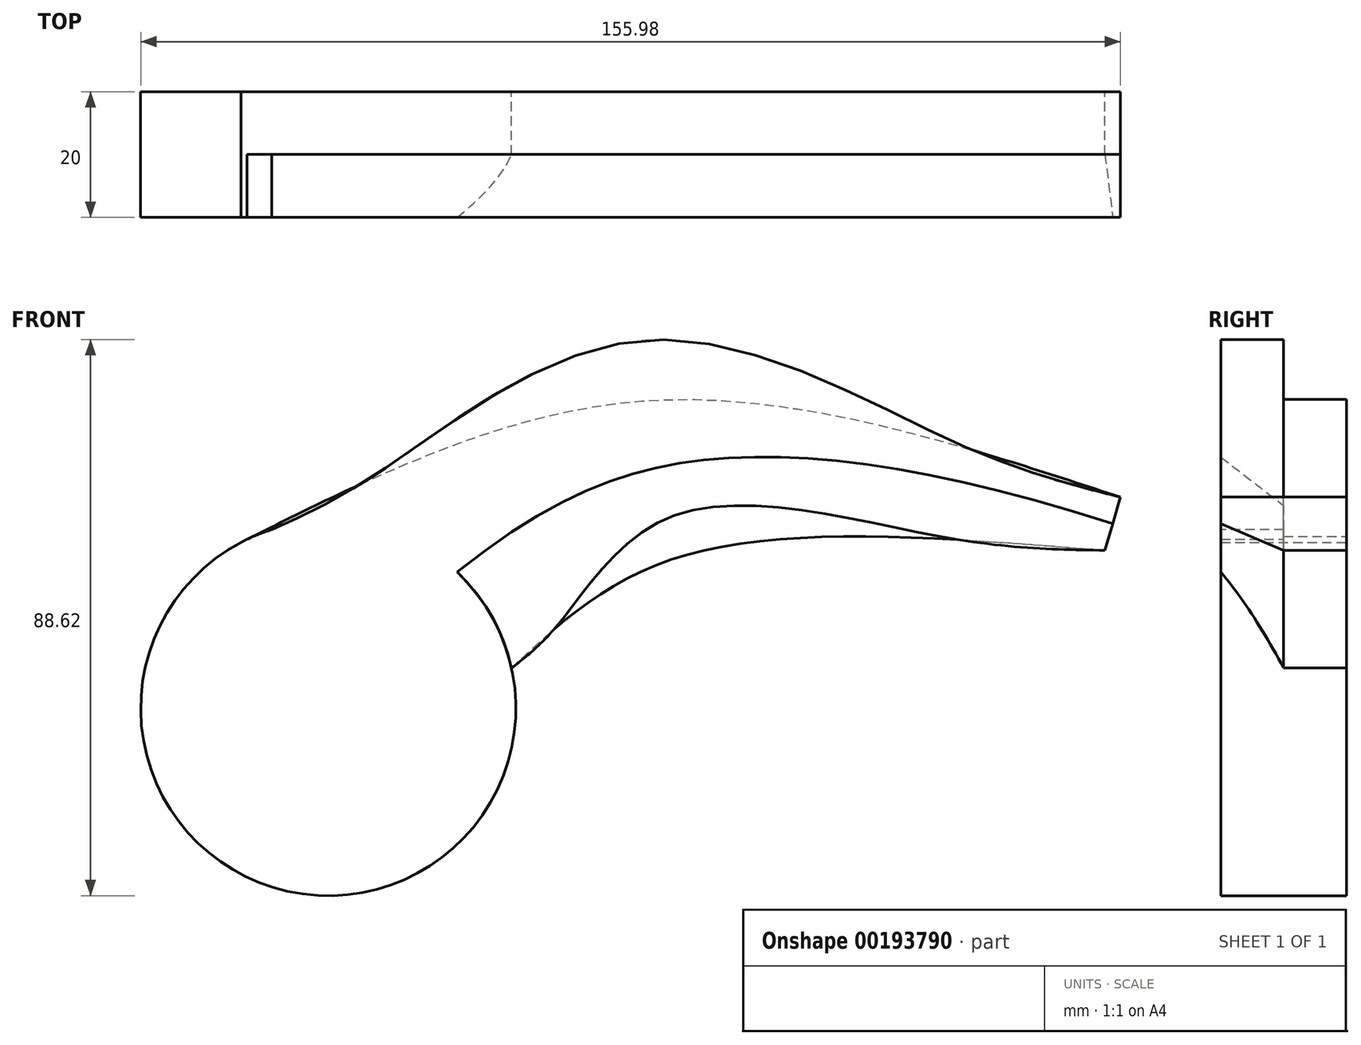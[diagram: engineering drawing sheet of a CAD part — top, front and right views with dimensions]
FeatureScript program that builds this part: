
annotation { "Feature Type Name" : "Feature", "Feature Type Description" : "" }
export const myFeature = defineFeature(function(context is Context, id is Id, definition is map)
    precondition{}
    {
        {
            var Q0;
            Q0=qCreatedBy(makeId("Front.planeOp"),FACE);
            var sketch = newSketch(context, id + "F0", { "sketchPlane" : qUnion([Q0])});
            skCircle(sketch, "E0", {"center": v(-61.69, -9.69) * mm, "radius": 29.87 * mm});
            skFitSpline(sketch, "E1", {"points": [v(-75.58, 16.75) * mm, v(-11.1, 39.34) * mm, v(64.43, 23.96) * mm], "startDerivative": vector(129.61, 65.17) * mm, "endDerivative": vector(150.18, -49.54) * mm});
            skFitSpline(sketch, "E2", {"points": [v(-32.52, -3.28) * mm, v(-5.98, 14.38) * mm, v(61.98, 15.5) * mm], "startDerivative": vector(55.34, 51.9) * mm, "endDerivative": vector(129.12, -10.46) * mm});
            skLineSegment(sketch, "E3", {"start": v(61.98, 15.5) * mm, "end": v(64.43, 23.96) * mm});
            skSolve(sketch);
        }
        {
            var Q0;
            {var subQ0=sQuery(id+"F0.wireOp",EDGE,"E0");var subQ1=makeQuery(id+"F0.imprint","INTERSECT",VERTEX,{"derivedFrom":[subQ0,sQuery(id+"F0.wireOp",EDGE,"E2")]});Q0=makeQuery(id+"F0.imprint","IMPRINT",FACE,{"disambiguationData":[TD([[makeQuery(id+"F0.imprint","IMPRINT",EDGE,{"disambiguationData":[TD([[subQ1,-1.0]])],"derivedFrom":subQ0}),1.0]])]});}
            cPlane(context, id + "F1", {"entities" : qUnion([Q0]), "cplaneType" : CPlaneType.OFFSET, "offset" : 10 * mm, "width" : 150 * mm, "height" : 150 * mm});
        }
        {
            var Q0;
            Q0=qCreatedBy(id+"F1.planeOp",FACE);
            cPlane(context, id + "F2", {"entities" : qUnion([Q0]), "cplaneType" : CPlaneType.OFFSET, "offset" : 10 * mm, "width" : 150 * mm, "height" : 150 * mm});
        }
        {
            var Q0;
            Q0=qCreatedBy(id+"F1.planeOp",FACE);
            var sketch = newSketch(context, id + "F3", { "sketchPlane" : qUnion([Q0])});
            skFitSpline(sketch, "E4.0", {"points": [v(-32.52, -3.28) * mm, v(-25.02, 3.75) * mm, v(-6.6, 21.05) * mm, v(36.44, 17.56) * mm, v(61.98, 15.5) * mm]});
            skFitSpline(sketch, "E4.2", {"points": [v(-75.58, 16.75) * mm, v(-54.63, 27.29) * mm, v(-11.4, 48.97) * mm, v(38.65, 32.47) * mm, v(64.43, 23.96) * mm]});
            skLineSegment(sketch, "E4.3", {"start": v(61.98, 15.5) * mm, "end": v(64.43, 23.96) * mm});
            skArc(sketch, "E5", {"start": v(-75.58, 16.75) * mm, "mid": v(-74.28, -36.77) * mm, "end": v(-32.52, -3.28) * mm});
            skSolve(sketch);
        }
        {
            var Q0;
            Q0=qCreatedBy(id+"F2.planeOp",FACE);
            var sketch = newSketch(context, id + "F4", { "sketchPlane" : qUnion([Q0])});
            skFitSpline(sketch, "E6.1", {"points": [v(-75.58, 16.75) * mm, v(-54.63, 27.29) * mm, v(-11.4, 48.97) * mm, v(38.65, 32.47) * mm, v(64.43, 23.96) * mm]});
            skFitSpline(sketch, "E7", {"points": [v(-41.18, 12.03) * mm, v(0, 30.05) * mm, v(63.2, 19.73) * mm], "startDerivative": vector(104.83, 83.31) * mm, "endDerivative": vector(149.14, -47.78) * mm});
            skArc(sketch, "E8", {"start": v(-75.58, 16.75) * mm, "mid": v(-65.75, -39.28) * mm, "end": v(-41.18, 12.03) * mm});
            skLineSegment(sketch, "E9", {"start": v(64.43, 23.96) * mm, "end": v(63.2, 19.73) * mm});
            skSolve(sketch);
        }
        {
            var Q0;
            Q0=makeQuery(id+"F3.imprint","IMPRINT",FACE,{"disambiguationData":[TD([[makeQuery(id+"F3.imprint","IMPRINT",EDGE,{"derivedFrom":sQuery(id+"F3.wireOp",EDGE,"E4.0")}),1.0]])]});
            var Q1;
            Q1=makeQuery(id+"F4.imprint","IMPRINT",FACE,{"disambiguationData":[TD([[makeQuery(id+"F4.imprint","IMPRINT",EDGE,{"derivedFrom":sQuery(id+"F4.wireOp",EDGE,"E6.1")}),-1.0]])]});
            loft(context, id + "F5", {"sheetProfilesArray" : [{ "sheetProfileEntities" : qUnion([Q0]) }, { "sheetProfileEntities" : qUnion([Q1]) }]});
        }
        {
            var Q0;
            {var subQ0=sQuery(id+"F0.wireOp",EDGE,"E2");Q0=makeQuery(id+"F0.imprint","IMPRINT",FACE,{"disambiguationData":[TD([[makeQuery(id+"F0.imprint","IMPRINT",EDGE,{"derivedFrom":subQ0}),1.0]])]});}
            extrude(context, id + "F6", {"entities" : qUnion([Q0]), "operationType" : NewBodyOperationType.ADD, "depth" : 10 * mm});
        }
        {
            var Q0;
            {var subQ0=sQuery(id+"F0.wireOp",EDGE,"E0");var subQ1=makeQuery(id+"F0.imprint","INTERSECT",VERTEX,{"derivedFrom":[subQ0,sQuery(id+"F0.wireOp",EDGE,"E2")]});Q0=makeQuery(id+"F0.imprint","IMPRINT",FACE,{"disambiguationData":[TD([[makeQuery(id+"F0.imprint","IMPRINT",EDGE,{"disambiguationData":[TD([[subQ1,-1.0]])],"derivedFrom":subQ0}),1.0]])]});}
            extrude(context, id + "F7", {"entities" : qUnion([Q0]), "operationType" : NewBodyOperationType.ADD, "depth" : 20 * mm});
        }
    });
